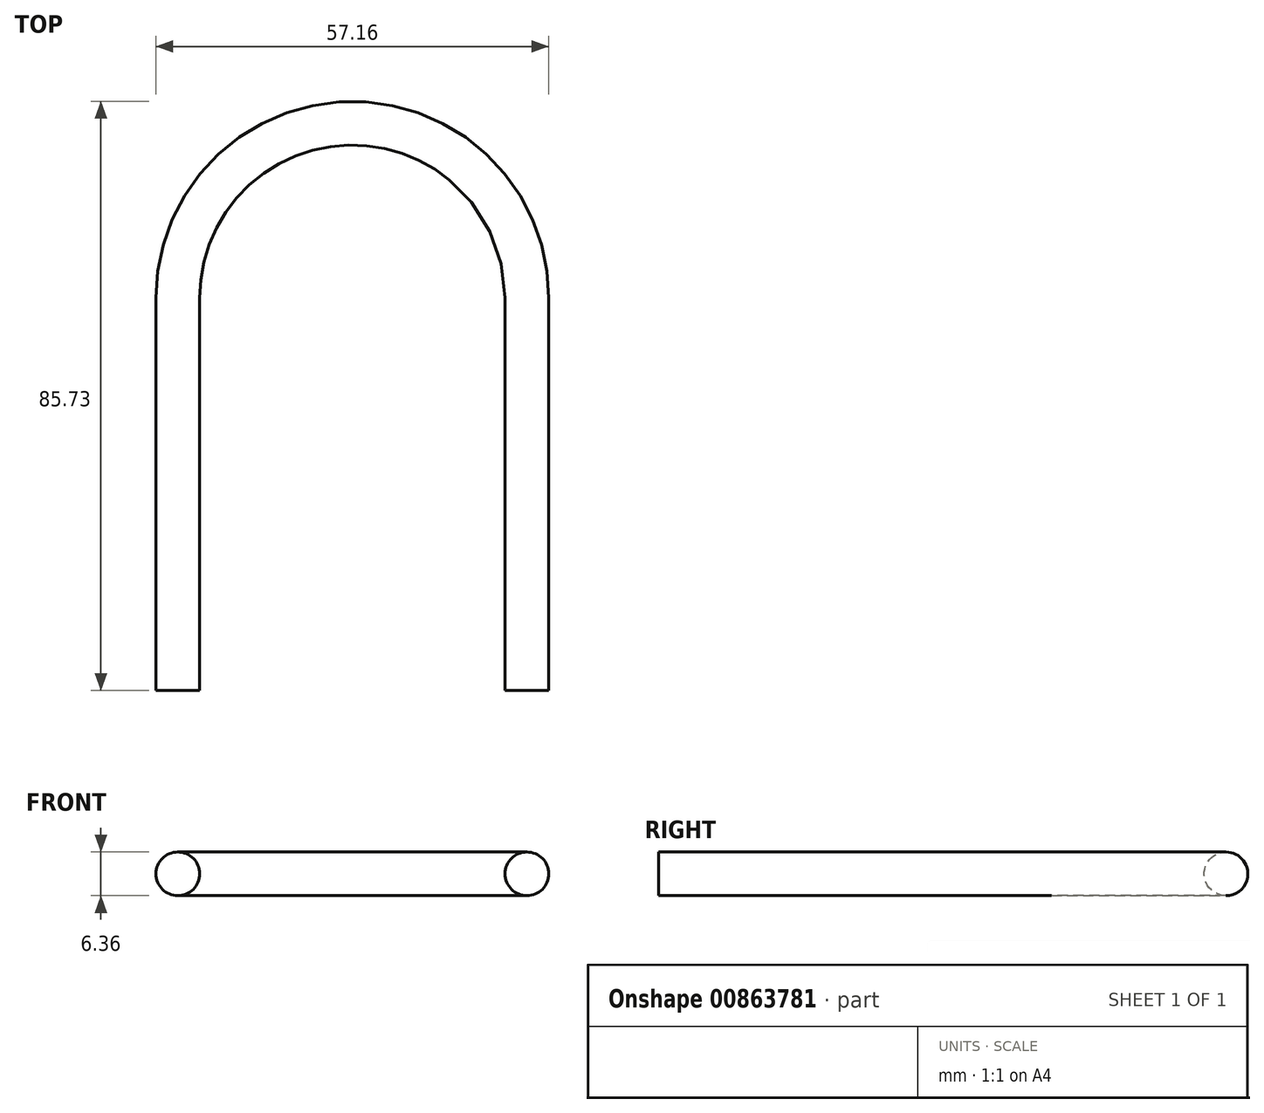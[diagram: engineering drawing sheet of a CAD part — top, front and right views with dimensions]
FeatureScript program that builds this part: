
annotation { "Feature Type Name" : "Feature", "Feature Type Description" : "" }
export const myFeature = defineFeature(function(context is Context, id is Id, definition is map)
    precondition{}
    {
        {
            var Q0;
            Q0=qCreatedBy(makeId("Top.planeOp"),FACE);
            var sketch = newSketch(context, id + "F0", { "sketchPlane" : qUnion([Q0])});
            skLineSegment(sketch, "E0", {"start": v(25.4, 0) * mm, "end": v(25.4, 57.15) * mm});
            skArc(sketch, "E1", {"start": v(25.4, 57.15) * mm, "mid": v(0, 82.55) * mm, "end": v(-25.4, 57.15) * mm});
            skLineSegment(sketch, "E2", {"start": v(-25.4, 57.15) * mm, "end": v(-25.4, 0) * mm});
            skSolve(sketch);
        }
        {
            var Q0;
            Q0=qCreatedBy(makeId("Front.planeOp"),FACE);
            var sketch = newSketch(context, id + "F1", { "sketchPlane" : qUnion([Q0])});
            skCircle(sketch, "E3", {"center": v(25.4, 0) * mm, "radius": 3.18 * mm});
            skSolve(sketch);
        }
        {
            var Q0;
            Q0=makeQuery(id+"F1.imprint","IMPRINT",FACE,{"disambiguationData":[TD([[makeQuery(id+"F1.imprint","IMPRINT",EDGE,{"derivedFrom":sQuery(id+"F1.wireOp",EDGE,"E3")}),1.0]])]});
            var Q1;
            Q1=sQuery(id+"F0.wireOp",EDGE,"E0");
            var Q2;
            Q2=sQuery(id+"F0.wireOp",EDGE,"E2");
            var Q3;
            Q3=sQuery(id+"F0.wireOp",EDGE,"E1");
            sweep(context, id + "F2", {"profiles" : qUnion([Q0]), "path" : qUnion([Q1, Q2, Q3])});
        }
    });
